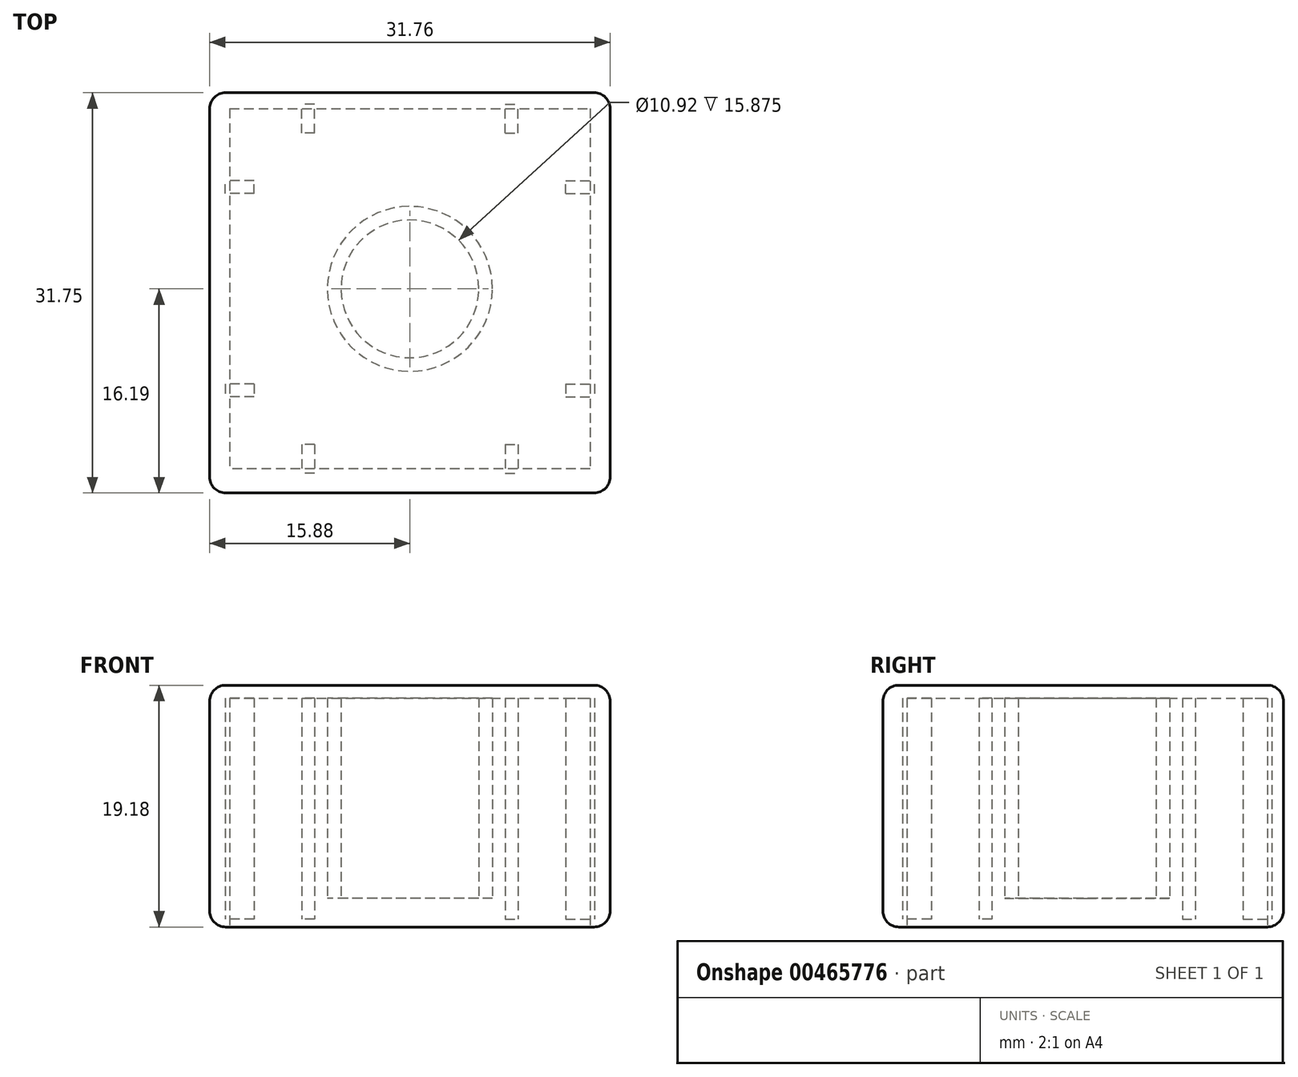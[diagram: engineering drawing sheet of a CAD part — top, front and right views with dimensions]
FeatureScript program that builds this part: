
annotation { "Feature Type Name" : "Feature", "Feature Type Description" : "" }
export const myFeature = defineFeature(function(context is Context, id is Id, definition is map)
    precondition{}
    {
        {
            var Q0;
            Q0=qCreatedBy(makeId("Top.planeOp"),FACE);
            var sketch = newSketch(context, id + "F0", { "sketchPlane" : qUnion([Q0])});
            skPoint(sketch, "E0", {"position": v(0, 16.87) * mm});
            skPoint(sketch, "E1", {"position": v(0, 15.88) * mm});
            skPoint(sketch, "E2", {"position": v(0, -14.88) * mm});
            skPoint(sketch, "E3", {"position": v(0, -15.88) * mm});
            skPoint(sketch, "E4", {"position": v(17.1, 0) * mm});
            skPoint(sketch, "E5", {"position": v(15.88, 0) * mm});
            skPoint(sketch, "E6", {"position": v(-15.88, 0) * mm});
            skPoint(sketch, "E7", {"position": v(15.64, 15.88) * mm});
            skPoint(sketch, "E8", {"position": v(15.88, 15.56) * mm});
            skPoint(sketch, "E9", {"position": v(-16.3, -15.88) * mm});
            skPoint(sketch, "E10", {"position": v(-15.88, -16.2) * mm});
            skLineSegment(sketch, "E11.bottom", {"start": v(-15.88, -16.2) * mm, "end": v(15.88, -16.2) * mm});
            skLineSegment(sketch, "E11.top", {"start": v(-15.88, 15.56) * mm, "end": v(15.88, 15.56) * mm});
            skLineSegment(sketch, "E11.left", {"start": v(-15.88, -16.2) * mm, "end": v(-15.88, 15.56) * mm});
            skLineSegment(sketch, "E11.right", {"start": v(15.88, -16.2) * mm, "end": v(15.88, 15.56) * mm});
            skSolve(sketch);
        }
        {
            var Q0;
            Q0=makeQuery(id+"F0.imprint","IMPRINT",FACE,{"disambiguationData":[TD([[makeQuery(id+"F0.imprint","IMPRINT",EDGE,{"derivedFrom":sQuery(id+"F0.wireOp",EDGE,"E11.bottom")}),1.0]])]});
            var sketch = newSketch(context, id + "F1", { "sketchPlane" : qUnion([Q0])});
            skPoint(sketch, "E12", {"position": v(14.77, 0) * mm});
            skPoint(sketch, "E13", {"position": v(14.29, 0) * mm});
            skPoint(sketch, "E14", {"position": v(-14.29, 0) * mm});
            skPoint(sketch, "E15", {"position": v(-14.29, -14.92) * mm});
            skPoint(sketch, "E16", {"position": v(-14.29, -14.29) * mm});
            skPoint(sketch, "E17", {"position": v(14.29, 14.33) * mm});
            skPoint(sketch, "E18", {"position": v(14.29, 14.29) * mm});
            skLineSegment(sketch, "E19.bottom", {"start": v(-14.29, -14.29) * mm, "end": v(14.29, -14.29) * mm});
            skLineSegment(sketch, "E19.top", {"start": v(-14.29, 14.29) * mm, "end": v(14.29, 14.29) * mm});
            skLineSegment(sketch, "E19.left", {"start": v(-14.29, -14.29) * mm, "end": v(-14.29, 14.29) * mm});
            skLineSegment(sketch, "E19.right", {"start": v(14.29, -14.29) * mm, "end": v(14.29, 14.29) * mm});
            skSolve(sketch);
        }
        {
            var Q0;
            Q0=makeQuery(id+"F1.imprint","IMPRINT",FACE,{"disambiguationData":[TD([[makeQuery(id+"F1.imprint","IMPRINT",EDGE,{"derivedFrom":sQuery(id+"F1.wireOp",EDGE,"E19.bottom")}),1.0]])]});
            var sketch = newSketch(context, id + "F2", { "sketchPlane" : qUnion([Q0])});
            skPoint(sketch, "E20", {"position": v(0, 0) * mm});
            skCircle(sketch, "E21", {"center": v(0, 0) * mm, "radius": 6.54 * mm});
            skSolve(sketch);
        }
        {
            var Q0;
            Q0=makeQuery(id+"F1.imprint","IMPRINT",FACE,{"disambiguationData":[TD([[makeQuery(id+"F1.imprint","IMPRINT",EDGE,{"derivedFrom":sQuery(id+"F1.wireOp",EDGE,"E19.bottom")}),1.0]])]});
            var sketch = newSketch(context, id + "F3", { "sketchPlane" : qUnion([Q0])});
            skPoint(sketch, "E22", {"position": v(0, 0) * mm});
            skCircle(sketch, "E23", {"center": v(0, 0) * mm, "radius": 5.46 * mm});
            skSolve(sketch);
        }
        {
            var Q0;
            Q0=makeQuery(id+"F1.imprint","IMPRINT",FACE,{"disambiguationData":[TD([[makeQuery(id+"F1.imprint","IMPRINT",EDGE,{"derivedFrom":sQuery(id+"F1.wireOp",EDGE,"E19.bottom")}),1.0]])]});
            var sketch = newSketch(context, id + "F4", { "sketchPlane" : qUnion([Q0])});
            skPoint(sketch, "E24", {"position": v(0, 1.02) * mm});
            skPoint(sketch, "E25", {"position": v(0, 0.95) * mm});
            skPoint(sketch, "E26", {"position": v(0, -0.95) * mm});
            skPoint(sketch, "E27", {"position": v(-0.23, 0) * mm});
            skPoint(sketch, "E28", {"position": v(-0.5, 0) * mm});
            skPoint(sketch, "E29", {"position": v(0.3, 0) * mm});
            skPoint(sketch, "E30", {"position": v(0.5, 0) * mm});
            skPoint(sketch, "E31", {"position": v(-0.5, -0.86) * mm});
            skPoint(sketch, "E32", {"position": v(-0.5, -1.5) * mm});
            skPoint(sketch, "E33", {"position": v(0.5, 0.79) * mm});
            skLineSegment(sketch, "E34.bottom", {"start": v(-0.5, -1.5) * mm, "end": v(0.5, -1.5) * mm});
            skLineSegment(sketch, "E34.top", {"start": v(-0.5, 0.79) * mm, "end": v(0.5, 0.79) * mm});
            skLineSegment(sketch, "E34.left", {"start": v(-0.5, -1.5) * mm, "end": v(-0.5, 0.79) * mm});
            skLineSegment(sketch, "E34.right", {"start": v(0.5, -1.5) * mm, "end": v(0.5, 0.79) * mm});
            skPoint(sketch, "E35", {"position": v(14.29, -8.12) * mm});
            skPoint(sketch, "E36", {"position": v(12.29, -8.12) * mm});
            skSolve(sketch);
        }
        {
            var Q0;
            Q0=qSketchRegion(id+"F0",true);
            extrude(context, id + "F5", {"entities" : qUnion([Q0]), "depth" : 19.18 * mm});
        }
        {
            var Q0;
            Q0=qSketchRegion(id+"F1",true);
            extrude(context, id + "F6", {"entities" : qUnion([Q0]), "operationType" : NewBodyOperationType.REMOVE, "depth" : 18.16 * mm, "hasSecondDirection" : true, "secondDirectionOppositeDirection" : true, "secondDirectionDepth" : 0.38 * mm});
        }
        {
            var Q0;
            Q0=qSketchRegion(id+"F2",true);
            extrude(context, id + "F7", {"entities" : qUnion([Q0]), "operationType" : NewBodyOperationType.ADD, "depth" : 15.88 * mm});
        }
        {
            var Q0;
            Q0=qSketchRegion(id+"F3",true);
            extrude(context, id + "F8", {"entities" : qUnion([Q0]), "operationType" : NewBodyOperationType.REMOVE, "depth" : 15.88 * mm, "hasSecondDirection" : true, "secondDirectionOppositeDirection" : true, "secondDirectionDepth" : 0.64 * mm});
        }
        {
            var Q0;
            Q0=makeQuery(id+"F7.opExtrude","SWEPT_BODY",BODY,{"disambiguationData":[OSD([sQuery(id+"F2.wireOp",EDGE,"E21")])]});
            transform(context, id + "F9", {"entities" : qUnion([Q0]), "transformType" : TransformType.TRANSLATION_3D, "dx" : 0 * mm, "dy" : 0 * mm, "dz" : 2.3 * mm, "makeCopy" : false});
        }
        {
            var Q0;
            Q0=makeQuery(id+"F4.imprint","IMPRINT",FACE,{"disambiguationData":[TD([[makeQuery(id+"F4.imprint","IMPRINT",EDGE,{"derivedFrom":sQuery(id+"F4.wireOp",EDGE,"E34.bottom")}),1.0]])]});
            extrude(context, id + "F10", {"entities" : qUnion([Q0]), "operationType" : NewBodyOperationType.ADD, "depth" : 17.53 * mm});
        }
        {
            var Q0;
            Q0=makeQuery(id+"F10.opExtrude","SWEPT_BODY",BODY,{"disambiguationData":[OSD([sQuery(id+"F4.wireOp",EDGE,"E34.bottom"),sQuery(id+"F4.wireOp",EDGE,"E34.top"),sQuery(id+"F4.wireOp",EDGE,"E34.left"),sQuery(id+"F4.wireOp",EDGE,"E34.right")])]});
            transform(context, id + "F11", {"entities" : qUnion([Q0]), "transformType" : TransformType.TRANSLATION_3D, "dx" : 8.06 * mm, "dy" : 13.86 * mm, "dz" : 0.64 * mm, "makeCopy" : false});
        }
        {
            var Q0;
            Q0=makeQuery(id+"F10.opExtrude","SWEPT_BODY",BODY,{"disambiguationData":[OSD([sQuery(id+"F4.wireOp",EDGE,"E34.bottom"),sQuery(id+"F4.wireOp",EDGE,"E34.top"),sQuery(id+"F4.wireOp",EDGE,"E34.left"),sQuery(id+"F4.wireOp",EDGE,"E34.right")])]});
            var Q1;
            Q1=qCreatedBy(makeId("Front.planeOp"),FACE);
            mirror(context, id + "F12", {"entities" : qUnion([Q0]), "mirrorPlane" : qUnion([Q1])});
        }
        {
            var Q0;
            Q0=makeQuery(id+"F12.opPattern","COPY",BODY,{"derivedFrom":makeQuery(id+"F10.opExtrude","SWEPT_BODY",BODY,{"disambiguationData":[OSD([sQuery(id+"F4.wireOp",EDGE,"E34.bottom"),sQuery(id+"F4.wireOp",EDGE,"E34.top"),sQuery(id+"F4.wireOp",EDGE,"E34.left"),sQuery(id+"F4.wireOp",EDGE,"E34.right")])]}),"instanceName":"1"});
            var Q1;
            Q1=makeQuery(id+"F10.opExtrude","SWEPT_BODY",BODY,{"disambiguationData":[OSD([sQuery(id+"F4.wireOp",EDGE,"E34.bottom"),sQuery(id+"F4.wireOp",EDGE,"E34.top"),sQuery(id+"F4.wireOp",EDGE,"E34.left"),sQuery(id+"F4.wireOp",EDGE,"E34.right")])]});
            var Q2;
            Q2=qCreatedBy(makeId("Right.planeOp"),FACE);
            mirror(context, id + "F13", {"entities" : qUnion([Q0, Q1]), "mirrorPlane" : qUnion([Q2])});
        }
        {
            var Q0;
            Q0=qCreatedBy(makeId("Front.planeOp"),FACE);
            var sketch = newSketch(context, id + "F14", { "sketchPlane" : qUnion([Q0])});
            skLineSegment(sketch, "E37", {"start": v(0, 40.9) * mm, "end": v(0, -32.36) * mm});
            skSolve(sketch);
        }
        {
            var Q0;
            Q0=makeQuery(id+"F12.opPattern","COPY",BODY,{"derivedFrom":makeQuery(id+"F10.opExtrude","SWEPT_BODY",BODY,{"disambiguationData":[OSD([sQuery(id+"F4.wireOp",EDGE,"E34.bottom"),sQuery(id+"F4.wireOp",EDGE,"E34.top"),sQuery(id+"F4.wireOp",EDGE,"E34.left"),sQuery(id+"F4.wireOp",EDGE,"E34.right")])]}),"instanceName":"1"});
            var Q1;
            Q1=makeQuery(id+"F13.opPattern","COPY",BODY,{"derivedFrom":makeQuery(id+"F12.opPattern","COPY",BODY,{"derivedFrom":makeQuery(id+"F10.opExtrude","SWEPT_BODY",BODY,{"disambiguationData":[OSD([sQuery(id+"F4.wireOp",EDGE,"E34.bottom"),sQuery(id+"F4.wireOp",EDGE,"E34.top"),sQuery(id+"F4.wireOp",EDGE,"E34.left"),sQuery(id+"F4.wireOp",EDGE,"E34.right")])]}),"instanceName":"1"}),"instanceName":"1"});
            var Q2;
            Q2=makeQuery(id+"F10.opExtrude","SWEPT_BODY",BODY,{"disambiguationData":[OSD([sQuery(id+"F4.wireOp",EDGE,"E34.bottom"),sQuery(id+"F4.wireOp",EDGE,"E34.top"),sQuery(id+"F4.wireOp",EDGE,"E34.left"),sQuery(id+"F4.wireOp",EDGE,"E34.right")])]});
            var Q3;
            Q3=makeQuery(id+"F13.opPattern","COPY",BODY,{"derivedFrom":makeQuery(id+"F10.opExtrude","SWEPT_BODY",BODY,{"disambiguationData":[OSD([sQuery(id+"F4.wireOp",EDGE,"E34.bottom"),sQuery(id+"F4.wireOp",EDGE,"E34.top"),sQuery(id+"F4.wireOp",EDGE,"E34.left"),sQuery(id+"F4.wireOp",EDGE,"E34.right")])]}),"instanceName":"1"});
            var Q4;
            Q4=sQuery(id+"F14.wireOp",EDGE,"E37");
            transform(context, id + "F15", {"entities" : qUnion([Q0, Q1, Q2, Q3]), "transformType" : TransformType.ROTATION, "transformAxis" : qUnion([Q4]), "angle" : 90 * degree, "makeCopy" : true});
        }
        {
            var Q0;
            Q0=makeQuery(id+"F5.opExtrude","CAP_EDGE",EDGE,{"disambiguationData":[OSD([sQuery(id+"F0.wireOp",EDGE,"E11.bottom")])],"isStart":false});
            var Q1;
            Q1=makeQuery(id+"F5.opExtrude","CAP_EDGE",EDGE,{"disambiguationData":[OSD([sQuery(id+"F0.wireOp",EDGE,"E11.left")])],"isStart":false});
            var Q2;
            Q2=makeQuery(id+"F5.opExtrude","CAP_EDGE",EDGE,{"disambiguationData":[OSD([sQuery(id+"F0.wireOp",EDGE,"E11.top")])],"isStart":false});
            var Q3;
            Q3=makeQuery(id+"F5.opExtrude","CAP_EDGE",EDGE,{"disambiguationData":[OSD([sQuery(id+"F0.wireOp",EDGE,"E11.right")])],"isStart":false});
            var Q4;
            Q4=makeQuery(id+"F5.opExtrude","SWEPT_EDGE",EDGE,{"disambiguationData":[OSD([sQuery(id+"F0.wireOp",EDGE,"E11.bottom"),sQuery(id+"F0.wireOp",EDGE,"E11.left")])]});
            var Q5;
            Q5=makeQuery(id+"F5.opExtrude","SWEPT_EDGE",EDGE,{"disambiguationData":[OSD([sQuery(id+"F0.wireOp",EDGE,"E11.bottom"),sQuery(id+"F0.wireOp",EDGE,"E11.right")])]});
            var Q6;
            Q6=makeQuery(id+"F5.opExtrude","SWEPT_EDGE",EDGE,{"disambiguationData":[OSD([sQuery(id+"F0.wireOp",EDGE,"E11.top"),sQuery(id+"F0.wireOp",EDGE,"E11.left")])]});
            var Q7;
            Q7=makeQuery(id+"F5.opExtrude","SWEPT_EDGE",EDGE,{"disambiguationData":[OSD([sQuery(id+"F0.wireOp",EDGE,"E11.top"),sQuery(id+"F0.wireOp",EDGE,"E11.right")])]});
            var Q8;
            Q8=makeQuery(id+"F5.opExtrude","CAP_EDGE",EDGE,{"disambiguationData":[OSD([sQuery(id+"F0.wireOp",EDGE,"E11.right")])],"isStart":true});
            var Q9;
            Q9=makeQuery(id+"F5.opExtrude","CAP_EDGE",EDGE,{"disambiguationData":[OSD([sQuery(id+"F0.wireOp",EDGE,"E11.bottom")])],"isStart":true});
            var Q10;
            Q10=makeQuery(id+"F5.opExtrude","CAP_EDGE",EDGE,{"disambiguationData":[OSD([sQuery(id+"F0.wireOp",EDGE,"E11.left")])],"isStart":true});
            var Q11;
            Q11=makeQuery(id+"F5.opExtrude","CAP_EDGE",EDGE,{"disambiguationData":[OSD([sQuery(id+"F0.wireOp",EDGE,"E11.top")])],"isStart":true});
            fillet(context, id + "F16", {"entities" : qUnion([Q0, Q1, Q2, Q3, Q4, Q5, Q6, Q7, Q8, Q9, Q10, Q11]), "radius" : 1.27 * mm, "tangentPropagation" : true, "allowEdgeOverflow" : false});
        }
    });
